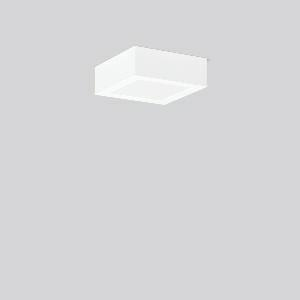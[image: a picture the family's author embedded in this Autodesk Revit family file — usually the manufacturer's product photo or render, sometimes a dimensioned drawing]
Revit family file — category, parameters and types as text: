
# Revit family: toledo_flat_square_a_672267_002_1_423a
name_source: partatom
category: Lighting Fixtures
units: mm (PartAtom-declared; Revit-internal decimal feet)

## family parameters
Cut with Voids When Loaded = No
Host = Face
Light Source = No
Part Type = Normal
Room Calculation Point = No
Round Connector Dimension = Use Diameter
Shared = No

## types (1)
- TOLEDO FLAT square A (1 x LED Modul 840, 730 lm, 4000)
    Apparent Load = 8 VA
    CIE Flux Codes = 49 80 96 100 100
    Color Rendering = 80
    Color Temperature = 4000
    Default Elevation = 1800 mm
    Description = Series: TOLEDO FLAT square
Ultra thin surface mounted downlight. For escape route illumination. Surface mounted housing: sheet steel, powder-coated. Square cover plate: die-cast aluminium, powder coated. Light guide and diffuser made of non-yellowing PMMA, opal matt. Driver integrated. Suitable for connection to central battery systems. 
Colour: white
Length: 172 mm
Width: 172 mm
Height: 58 mm
Weight: 1.33 kg
Operating mode: maintained power mode
Lamp: LED
Socket: without socket
Colour temperature: 4000K
Colour rendering index (CRI): 80
System power: 8 W
Rated luminous flux: 730 lm
Luminous flux, emergency: 730 lm
System power, emergency: 8 W
Control gear: Regulated power supply
Protection class: I
Type of protection: IP 40
    Height = 58 mm
    Lamp = 1 x LED Modul 840
    Lamp Light Flux = 730 lm
    Lamp count = 1
    Length = 172 mm
    Lifetime = 50000 h
    Luminous efficacy = 91 lm/W
    Manufacturer = RZB
    ModVariant = No
    Model = 672267.002.1
    Mounting Place = Ceiling
    Mounting Type = Surface mounted
    Number of Poles = 1
    OnlyDefault = Yes
    Power Factor = 1
    Product Name = TOLEDO FLAT square A
    Product group = Surface mounted downlights
    ProductGroupID = 302
    Protection Class = Protection class I
    Protection Degree = IP 40
    RLX_Detail_Level = 1
    RLX_Emergency_Light_Flux = 730 lm
    RLX_Emergency_Type = 3
    RLX_Emergency_Type_DB = Yes
    RlxData = <blob elided: 14045 chars, md5=e1e5d539>
    Socket = socket
    Standby Power = 0 W
    System Light Flux = 730 lm
    System Power = 8 W
    Type Comments = Product without accessories
    Type Image = 901552.002.jpg
    URL = http://relux.com
    VarID = ---
    Voltage = 230 V
    Voltage Range = 220-240 V
    Weight = 0.00 kg
    Width = 172 mm

## geometry (parser evidence)
native form markers: Sweep x11
no freeform markers — native parametric forms only
